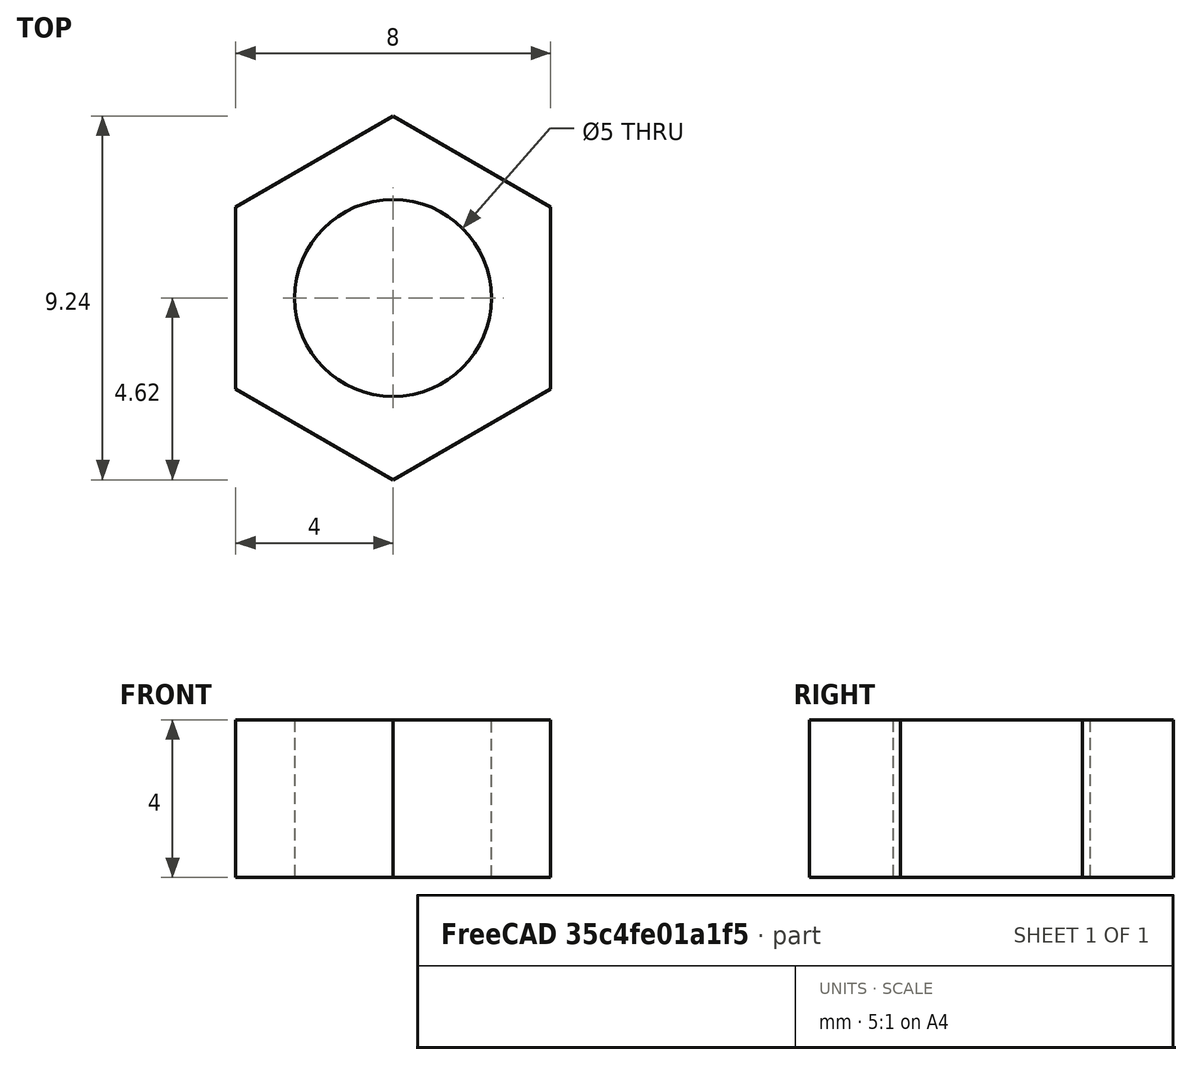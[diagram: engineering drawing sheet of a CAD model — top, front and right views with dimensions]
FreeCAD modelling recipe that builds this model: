
FCSTD DOCUMENT  (FreeCAD 0.16R6706 (Git))
Label: m5 nut
License: All rights reserved
LicenseURL: http://en.wikipedia.org/wiki/All_rights_reserved
objects: Sketcher::SketchObject×1, PartDesign::Pad×1
note: 3 computed .brp shape members not serialized (recipe doc carries the construction recipe); baked Part::Feature solids carry a one-line shape summary decoded from their .brp

FEATURE [Sketcher::SketchObject] Sketch
  sketch-geometry (8):
    g0: LineSegment StartX=0 StartY=4.6188 StartZ=0 EndX=-4 EndY=2.3094 EndZ=0
    g1: LineSegment StartX=-4 StartY=2.3094 StartZ=0 EndX=-4 EndY=-2.3094 EndZ=0
    g2: LineSegment StartX=-4 StartY=-2.3094 StartZ=0 EndX=0 EndY=-4.6188 EndZ=0
    g3: LineSegment StartX=0 StartY=-4.6188 StartZ=0 EndX=4 EndY=-2.3094 EndZ=0
    g4: LineSegment StartX=4 StartY=-2.3094 StartZ=0 EndX=4 EndY=2.3094 EndZ=0
    g5: LineSegment StartX=4 StartY=2.3094 StartZ=0 EndX=0 EndY=4.6188 EndZ=0
    g6: Circle [constr] CenterX=0 CenterY=0 CenterZ=0 NormalX=0 NormalY=0 NormalZ=1 Radius=4.6188
    g7: Circle CenterX=0 CenterY=0 CenterZ=0 NormalX=0 NormalY=0 NormalZ=1 Radius=2.5
  constraints (18):
    c: Coincident(g0,g1)
    c: Coincident(g1,g2)
    c: Coincident(g2,g3)
    c: Coincident(g3,g4)
    c: Coincident(g4,g5)
    c: Coincident(g5,g0)
    c: Equal(g0, g1-g5) x5
    c: PointOnObject(g0,g6)
    c: PointOnObject(g1,g6)
    c: PointOnObject(g2,g6)
    c: PointOnObject(g3,g6)
    c: PointOnObject(g4,g6)
    c: PointOnObject(g5,g6)
    c: Coincident(g6,g-1)
    c: Vertical(g4)
    c: DistanceX(g0,g4) = 8
    c: Coincident(g7,g-1)
    c: Radius(g7) = 2.5
FEATURE [PartDesign::Pad] Pad
  Length = 4
  Length2 = 100
  Sketch = -> Sketch
  Type = 0
